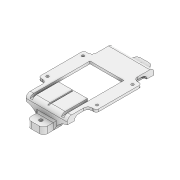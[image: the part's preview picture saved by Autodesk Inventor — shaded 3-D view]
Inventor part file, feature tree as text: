
AUTODESK INVENTOR PART (.ipt)
format: ipt  version: 2020 (Build 240168000, 168)  size: 341,504 bytes
history: native  units: mm
features: extrude x10, sketch x10, fillet x7, plane x1, mirror x1
ambient origin geometry x8: Origin, YZ Plane, XZ Plane, XY Plane, X Axis, Y Axis, Z Axis, Center Point
bodies: Solid1 (feature_tree)
feature tree (29):
  extrude  "Extrusion1"  Depth=105.0mm
  extrude  "Extrusion2"  Depth=3.0mm
  extrude  "Extrusion3"  Depth=48.327mm
  extrude  "Extrusion4"  Depth=88.0mm
  extrude  "Extrusion5"  Depth=41.0mm
  extrude  "Extrusion6"  Depth=18.8mm TaperAngle=0.0deg
  extrude  "Extrusion7"  Depth=3.0mm
  fillet  "Fillet1"  Radius=3.0mm
  fillet  "Fillet2"  Radius=4.0mm
  fillet  "Fillet3"  Radius=4.0mm
  fillet  "Fillet4"  Radius=5.0mm
  extrude  "Extrusion8"  Depth=10.0mm
  fillet  "Fillet5"  Radius=55.0mm
  extrude  "Extrusion9"  Depth=3.1mm
  extrude  "Extrusion10"  Depth=2.0mm
  plane  "Work Plane1"
  mirror  "Mirror1"
  fillet  "Fillet6"  Radius=3.0mm
  fillet  "Fillet7"  Radius=3.0mm
  sketch  "Sketch1"  dims[d0=50.0mm d1=105.0mm]
  sketch  "Sketch2"  dims[d2=3.0mm d3=3.0mm]
  sketch  "Sketch3"  dims[d4=96.564mm d5=48.327mm]
  sketch  "Sketch4"  dims[d6=3.0mm d7=0.0mm d9=88.0mm]
  sketch  "Sketch5"  dims[d12=17.0mm d13=0.0mm d14=41.0mm]
  sketch  "Sketch6"  dims[d15=41.0mm d16=18.8mm d17=0.0mm]
  sketch  "Sketch7"  dims[d18=3.0mm d19=3.0mm d20=3.0mm d21=0.0mm d22=4.0mm d23=4.0mm d24=5.0mm d25=0.0mm]
  sketch  "Sketch8"  dims[d26=3.0mm d27=0.0mm d28=10.0mm d29=55.0mm]
  sketch  "Sketch9"  dims[d30=3.1mm d31=3.1mm]
  sketch  "Sketch10"  dims[d32=6.0mm d33=6.0mm d34=3.0mm d35=0.0mm d36=3.0mm d37=5.0mm d38=5.0mm d39=5.0mm d40=1.5mm d41=0.75mm d42=1.0mm d43=0.0mm d44=2.0mm d45=12.0mm d46=15.0mm d47=18.0mm d48=116.75mm d49=0.0mm d50=44.0mm d51=14.0mm d52=4.1mm d53=8.0mm d54=6.0mm d55=0.0mm d56=0.0mm d57=5.0mm d58=2.0mm]
